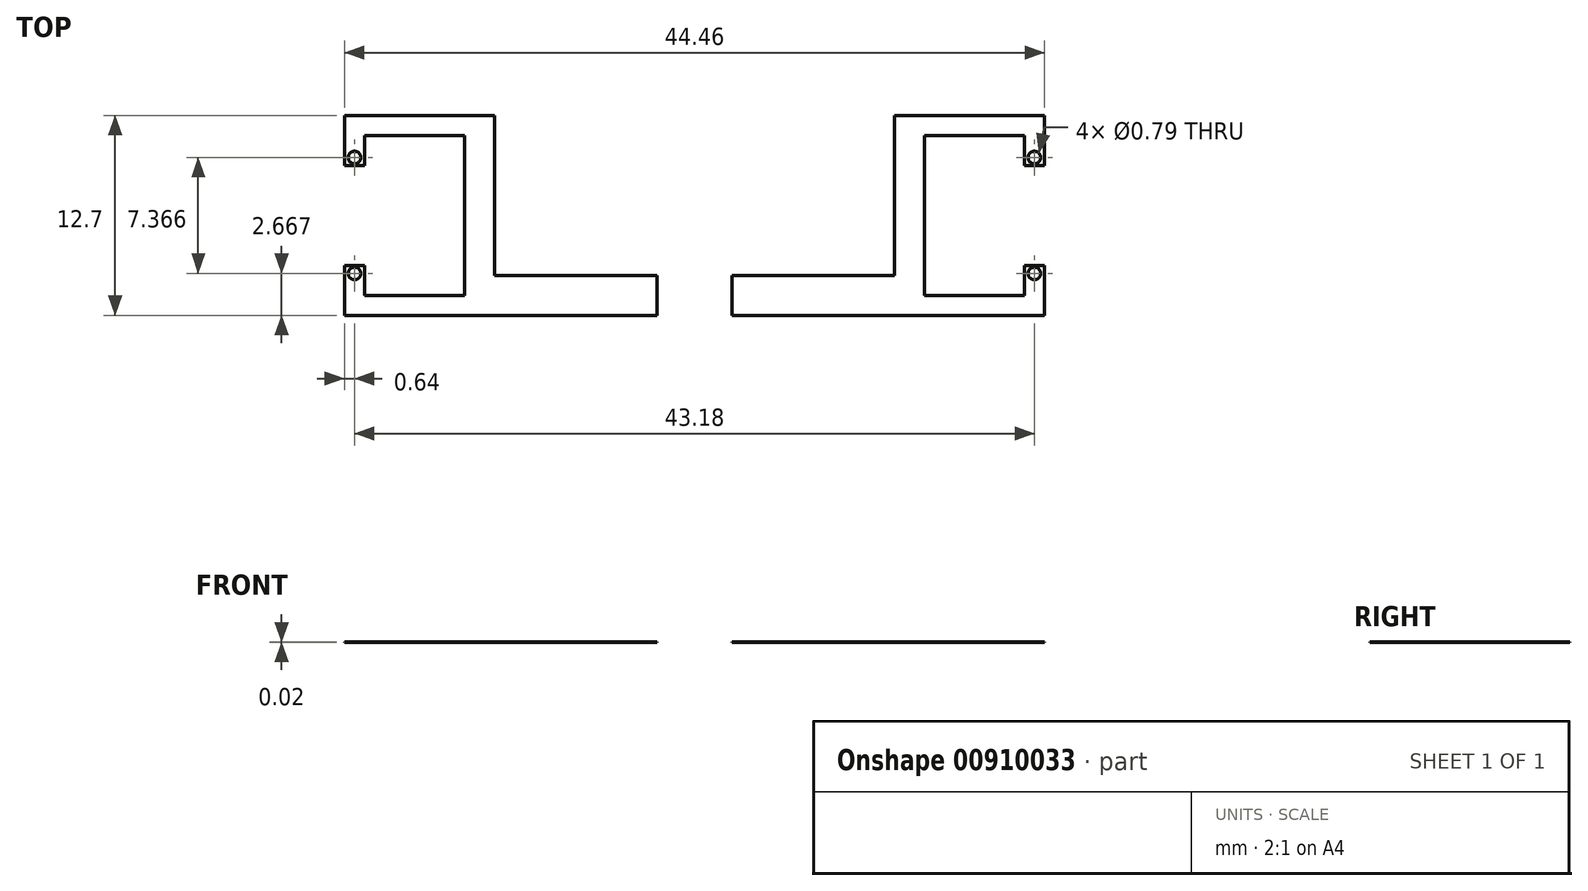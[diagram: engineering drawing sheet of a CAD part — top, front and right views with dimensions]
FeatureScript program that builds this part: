
annotation { "Feature Type Name" : "Feature", "Feature Type Description" : "" }
export const myFeature = defineFeature(function(context is Context, id is Id, definition is map)
    precondition{}
    {
        {
            var Q0;
            Q0=qCreatedBy(makeId("Top.planeOp"),FACE);
            var sketch = newSketch(context, id + "F0", { "sketchPlane" : qUnion([Q0])});
            skLineSegment(sketch, "E0", {"start": v(-22.23, 11.43) * mm, "end": v(-12.7, 11.43) * mm});
            skLineSegment(sketch, "E1", {"start": v(-12.7, 11.43) * mm, "end": v(-12.7, -1.27) * mm});
            skLineSegment(sketch, "E2", {"start": v(-12.7, -1.27) * mm, "end": v(-22.23, -1.27) * mm});
            skLineSegment(sketch, "E3", {"start": v(-22.23, -1.27) * mm, "end": v(-22.23, 1.9) * mm});
            skLineSegment(sketch, "E4", {"start": v(-22.23, 1.9) * mm, "end": v(-20.96, 1.9) * mm});
            skLineSegment(sketch, "E5", {"start": v(-20.96, 1.9) * mm, "end": v(-20.96, 0) * mm});
            skLineSegment(sketch, "E6", {"start": v(-20.96, 0) * mm, "end": v(-14.6, 0) * mm});
            skLineSegment(sketch, "E7", {"start": v(-14.6, 0) * mm, "end": v(-14.6, 10.16) * mm});
            skLineSegment(sketch, "E8", {"start": v(-14.6, 10.16) * mm, "end": v(-20.96, 10.16) * mm});
            skLineSegment(sketch, "E9", {"start": v(-20.96, 10.16) * mm, "end": v(-20.96, 8.26) * mm});
            skLineSegment(sketch, "E10", {"start": v(-20.96, 8.25) * mm, "end": v(-22.23, 8.25) * mm});
            skLineSegment(sketch, "E11", {"start": v(-22.23, 8.26) * mm, "end": v(-22.23, 11.43) * mm});
            skLineSegment(sketch, "E12.MirrorCS", {"start": v(14.6, 0) * mm, "end": v(14.6, 10.16) * mm});
            skLineSegment(sketch, "E13.MirrorCS", {"start": v(12.7, 11.43) * mm, "end": v(12.7, -1.27) * mm});
            skLineSegment(sketch, "E14.MirrorCS", {"start": v(20.96, 0) * mm, "end": v(14.6, 0) * mm});
            skLineSegment(sketch, "E15.MirrorCS", {"start": v(12.7, -1.27) * mm, "end": v(22.23, -1.27) * mm});
            skLineSegment(sketch, "E16.MirrorCS", {"start": v(22.23, -1.27) * mm, "end": v(22.23, 1.9) * mm});
            skLineSegment(sketch, "E17.MirrorCS", {"start": v(20.96, 1.9) * mm, "end": v(20.96, 0) * mm});
            skLineSegment(sketch, "E18.MirrorCS", {"start": v(22.23, 1.9) * mm, "end": v(20.96, 1.9) * mm});
            skLineSegment(sketch, "E19.MirrorCS", {"start": v(20.96, 8.25) * mm, "end": v(22.23, 8.25) * mm});
            skLineSegment(sketch, "E20.MirrorCS", {"start": v(22.23, 8.26) * mm, "end": v(22.23, 11.43) * mm});
            skLineSegment(sketch, "E21.MirrorCS", {"start": v(20.96, 10.16) * mm, "end": v(20.96, 8.26) * mm});
            skLineSegment(sketch, "E22.MirrorCS", {"start": v(14.6, 10.16) * mm, "end": v(20.96, 10.16) * mm});
            skLineSegment(sketch, "E23.MirrorCS", {"start": v(22.23, 11.43) * mm, "end": v(12.7, 11.43) * mm});
            skCircle(sketch, "E24", {"center": v(-21.6, 8.76) * mm, "radius": 0.4 * mm});
            skCircle(sketch, "E25", {"center": v(-21.6, 1.4) * mm, "radius": 0.4 * mm});
            skCircle(sketch, "E26.MirrorC", {"center": v(21.6, 8.76) * mm, "radius": 0.4 * mm});
            skCircle(sketch, "E27.MirrorC", {"center": v(21.6, 1.4) * mm, "radius": 0.4 * mm});
            skLineSegment(sketch, "E28", {"start": v(-12.7, 1.27) * mm, "end": v(12.7, 1.27) * mm});
            skLineSegment(sketch, "E29", {"start": v(-12.7, -1.27) * mm, "end": v(12.7, -1.27) * mm});
            skCircle(sketch, "E30", {"center": v(0, -64.77) * mm, "radius": 0.8 * mm});
            skPoint(sketch, "E31.visualSharp", {"position": v(0, -71.12) * mm});
            skArc(sketch, "E32.filletArc", {"start": v(-0.62, -67.68) * mm, "mid": v(0, -68.2) * mm, "end": v(0.62, -67.68) * mm});
            skSolve(sketch);
        }
        {
            var Q0;
            {var subQ0=sQuery(id+"F0.wireOp",EDGE,"E0");Q0=makeQuery(id+"F0.imprint","IMPRINT",FACE,{"disambiguationData":[TD([[makeQuery(id+"F0.imprint","IMPRINT",EDGE,{"derivedFrom":subQ0}),-1.0]])]});}
            var Q1;
            {var subQ4=sQuery(id+"F0.wireOp",EDGE,"E28");Q1=makeQuery(id+"F0.imprint","IMPRINT",FACE,{"disambiguationData":[TD([[makeQuery(id+"F0.imprint","IMPRINT",EDGE,{"derivedFrom":subQ4}),-1.0]])]});}
            var Q2;
            Q2=makeQuery(id+"F0.imprint","IMPRINT",FACE,{"disambiguationData":[TD([[makeQuery(id+"F0.imprint","IMPRINT",EDGE,{"derivedFrom":sQuery(id+"F0.wireOp",EDGE,"E12.MirrorCS")}),1.0]])]});
            var Q3;
            {var subQ8=sQuery(id+"F0.wireOp",EDGE,"1PjGuBIR-9Pv4-rMLk-RCzl-I51GPpE8k7TI");Q3=makeQuery(id+"F0.imprint","IMPRINT",FACE,{"disambiguationData":[TD([[makeQuery(id+"F0.imprint","IMPRINT",EDGE,{"derivedFrom":subQ8}),1.0]])]});}
            var Q4;
            {var subQ0=sQuery(id+"F0.wireOp",EDGE,"OXakiHan-UgVx-rdoX-cPiA-IruJlf0qgsDQ");Q4=makeQuery(id+"F0.imprint","IMPRINT",FACE,{"disambiguationData":[TD([[makeQuery(id+"F0.imprint","IMPRINT",EDGE,{"derivedFrom":subQ0}),1.0]])]});}
            var Q5;
            {var subQ0=sQuery(id+"F0.wireOp",EDGE,"OmNe6PKq-3gdd-MlfY-zTIg-1ZM3LVirDwKM");Q5=makeQuery(id+"F0.imprint","IMPRINT",FACE,{"disambiguationData":[TD([[makeQuery(id+"F0.imprint","IMPRINT",EDGE,{"derivedFrom":subQ0}),1.0]])]});}
            extrude(context, id + "F1", {"entities" : qUnion([Q0, Q1, Q2, Q3, Q4, Q5]), "endBound" : BoundingType.SYMMETRIC, "depth" : 3 / 203.2 * mm, "offsetDistance" : 25.4 * mm});
        }
        {
            var Q0;
            Q0=makeQuery(id+"F1.opExtrude","SWEPT_FACE",FACE,{"disambiguationData":[OSD([sQuery(id+"F0.wireOp",EDGE,"E28")])]});
            var sketch = newSketch(context, id + "F2", { "sketchPlane" : qUnion([Q0])});
            skCircle(sketch, "E33", {"center": v(0, 0) * mm, "radius": 2.38 * mm});
            skSolve(sketch);
        }
        {
            var Q0;
            Q0=makeQuery(id+"F2.imprint","IMPRINT",FACE,{"disambiguationData":[TD([[makeQuery(id+"F2.imprint","IMPRINT",EDGE,{"derivedFrom":sQuery(id+"F2.wireOp",EDGE,"E33")}),1.0]])]});
            extrude(context, id + "F3", {"entities" : qUnion([Q0]), "operationType" : NewBodyOperationType.REMOVE, "oppositeDirection" : true, "depth" : 5.97 * mm, "offsetDistance" : 25.4 * mm});
        }
    });
